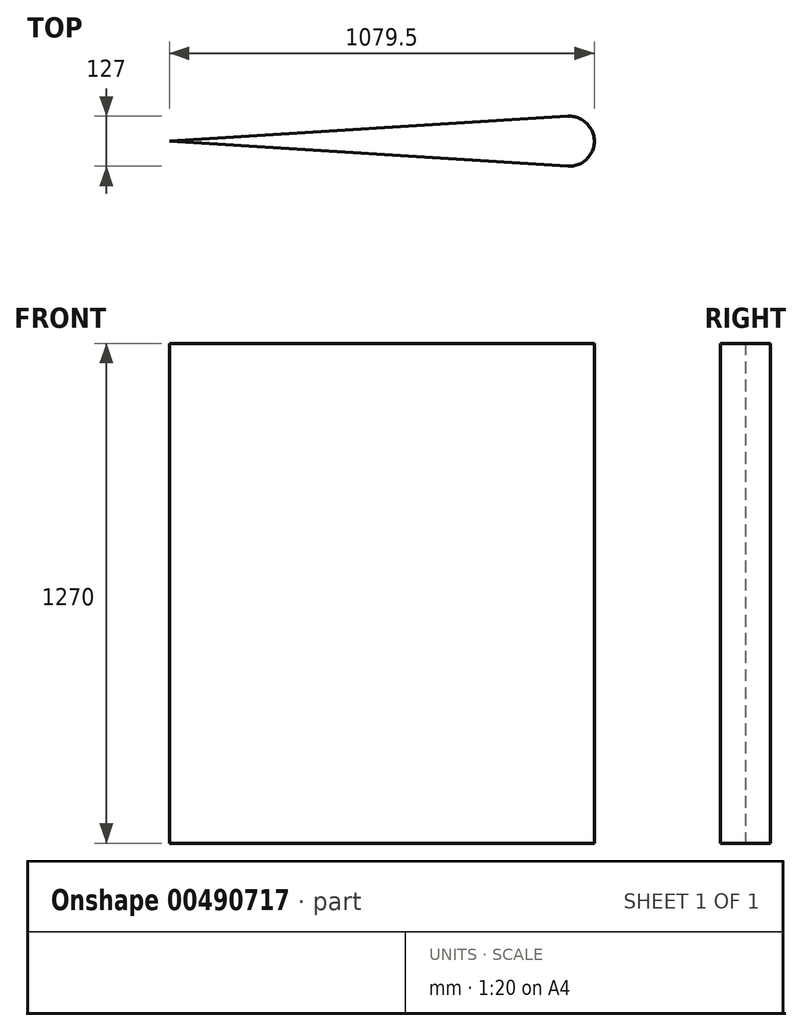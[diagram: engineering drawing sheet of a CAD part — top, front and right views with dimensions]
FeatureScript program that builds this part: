
annotation { "Feature Type Name" : "Feature", "Feature Type Description" : "" }
export const myFeature = defineFeature(function(context is Context, id is Id, definition is map)
    precondition{}
    {
        {
            var Q0;
            Q0=qCreatedBy(makeId("Top.planeOp"),FACE);
            var sketch = newSketch(context, id + "F0", { "sketchPlane" : qUnion([Q0])});
            skCircle(sketch, "E0", {"center": v(94.07, 0) * mm, "radius": 31.75 * mm});
            skCircle(sketch, "E1", {"center": v(602.07, 0) * mm, "radius": 63.5 * mm});
            skLineSegment(sketch, "E2", {"start": v(94.07, 0) * mm, "end": v(602.07, 0) * mm});
            skLineSegment(sketch, "E3", {"start": v(-537.2, -7.72) * mm, "end": v(1364.07, 111.34) * mm});
            skLineSegment(sketch, "E4", {"start": v(-537.2, 7.72) * mm, "end": v(1364.07, -111.34) * mm});
            skLineSegment(sketch, "E5", {"start": v(1364.07, 111.34) * mm, "end": v(1364.07, -111.34) * mm});
            skLineSegment(sketch, "E6", {"start": v(602.07, 0) * mm, "end": v(1364.07, 0) * mm});
            skPoint(sketch, "E6.endSnap0", {"position": v(1364.07, 0) * mm});
            skSolve(sketch);
        }
        {
            var Q0;
            {var subQ0=sQuery(id+"F0.wireOp",EDGE,"E0");var subQ1=makeQuery(id+"F0.imprint","INTERSECT",VERTEX,{"derivedFrom":[subQ0,sQuery(id+"F0.wireOp",EDGE,"E3")]});Q0=makeQuery(id+"F0.imprint","IMPRINT",FACE,{"disambiguationData":[TD([[makeQuery(id+"F0.imprint","IMPRINT",EDGE,{"disambiguationData":[TD([[subQ1,1.0]])],"derivedFrom":subQ0}),1.0]])]});}
            var Q1;
            {var subQ0=sQuery(id+"F0.wireOp",EDGE,"E3");var subQ1=sQuery(id+"F0.wireOp",EDGE,"E0");var subQ2=makeQuery(id+"F0.imprint","INTERSECT",VERTEX,{"derivedFrom":[subQ1,subQ0]});Q1=makeQuery(id+"F0.imprint","IMPRINT",FACE,{"disambiguationData":[TD([[makeQuery(id+"F0.imprint","IMPRINT",EDGE,{"disambiguationData":[TD([[subQ2,1.0]])],"derivedFrom":subQ1}),-1.0]])]});}
            var Q2;
            {var subQ0=sQuery(id+"F0.wireOp",EDGE,"E2");var subQ1=sQuery(id+"F0.wireOp",EDGE,"E0");var subQ2=makeQuery(id+"F0.imprint","INTERSECT",VERTEX,{"derivedFrom":[subQ1,subQ0]});Q2=makeQuery(id+"F0.imprint","IMPRINT",FACE,{"disambiguationData":[TD([[makeQuery(id+"F0.imprint","IMPRINT",EDGE,{"disambiguationData":[TD([[subQ2,1.0]])],"derivedFrom":subQ1}),-1.0]])]});}
            var Q3;
            {var subQ0=sQuery(id+"F0.wireOp",EDGE,"E1");var subQ1=makeQuery(id+"F0.imprint","INTERSECT",VERTEX,{"derivedFrom":[subQ0,sQuery(id+"F0.wireOp",EDGE,"E4")]});Q3=makeQuery(id+"F0.imprint","IMPRINT",FACE,{"disambiguationData":[TD([[makeQuery(id+"F0.imprint","IMPRINT",EDGE,{"disambiguationData":[TD([[subQ1,1.0]])],"derivedFrom":subQ0}),1.0]])]});}
            var Q4;
            {var subQ0=sQuery(id+"F0.wireOp",EDGE,"E1");var subQ1=makeQuery(id+"F0.imprint","INTERSECT",VERTEX,{"derivedFrom":[subQ0,sQuery(id+"F0.wireOp",EDGE,"E3")]});Q4=makeQuery(id+"F0.imprint","IMPRINT",FACE,{"disambiguationData":[TD([[makeQuery(id+"F0.imprint","IMPRINT",EDGE,{"disambiguationData":[TD([[subQ1,1.0]])],"derivedFrom":subQ0}),1.0]])]});}
            var Q5;
            {var subQ0=sQuery(id+"F0.wireOp",EDGE,"E3");var subQ1=sQuery(id+"F0.wireOp",EDGE,"E0");var subQ2=makeQuery(id+"F0.imprint","INTERSECT",VERTEX,{"derivedFrom":[subQ1,subQ0]});Q5=makeQuery(id+"F0.imprint","IMPRINT",FACE,{"disambiguationData":[TD([[makeQuery(id+"F0.imprint","IMPRINT",EDGE,{"disambiguationData":[TD([[subQ2,-1.0]])],"derivedFrom":subQ1}),-1.0]])]});}
            extrude(context, id + "F1", {"entities" : qUnion([Q0, Q1, Q2, Q3, Q4, Q5]), "depth" : 1270 * mm});
        }
    });
